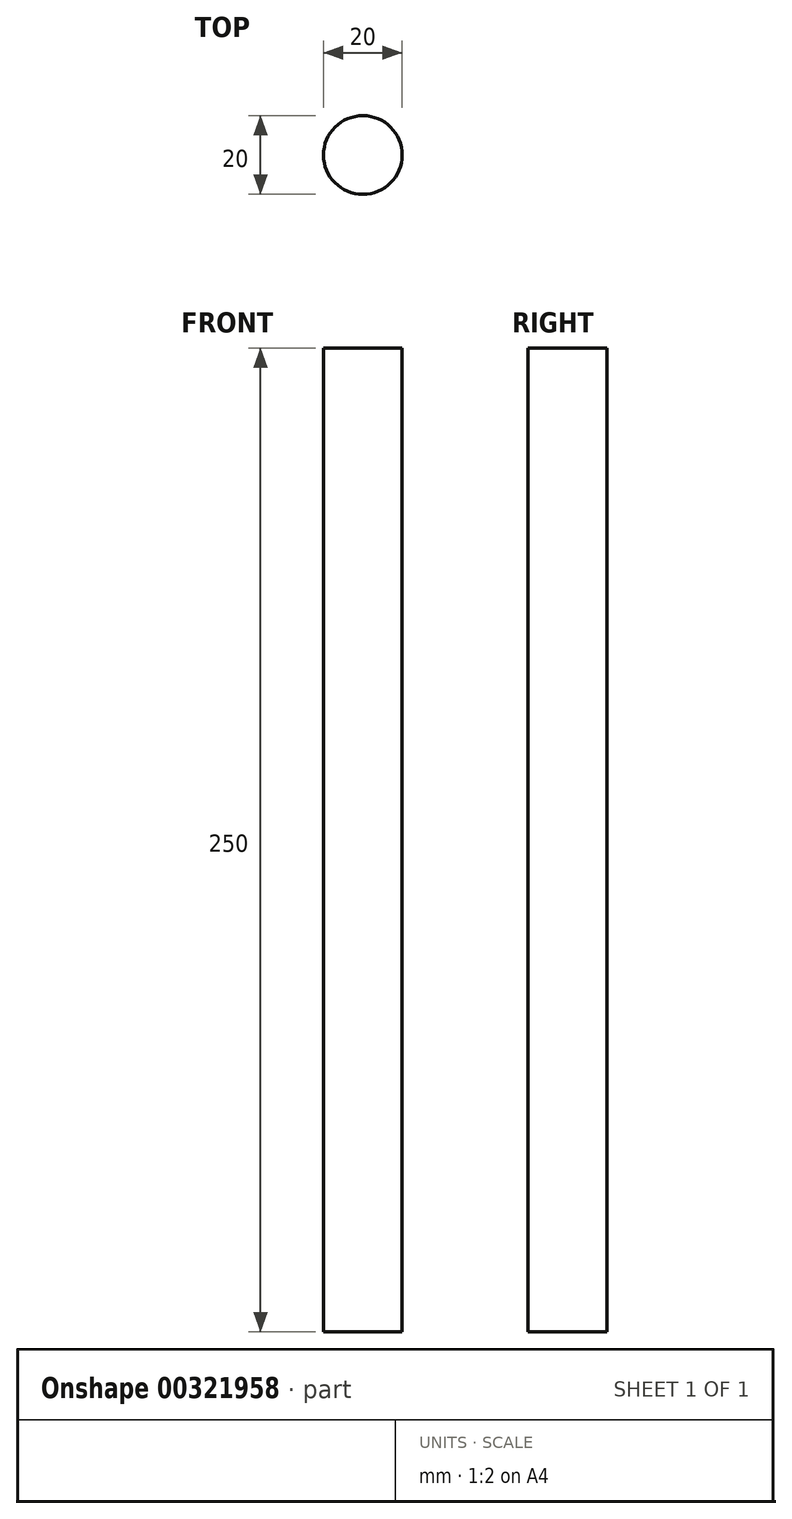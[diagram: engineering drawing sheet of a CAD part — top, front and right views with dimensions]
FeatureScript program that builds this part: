
annotation { "Feature Type Name" : "Feature", "Feature Type Description" : "" }
export const myFeature = defineFeature(function(context is Context, id is Id, definition is map)
    precondition{}
    {
        {
            var Q0;
            Q0=qCreatedBy(makeId("Top.planeOp"),FACE);
            var sketch = newSketch(context, id + "F0", { "sketchPlane" : qUnion([Q0])});
            skCircle(sketch, "E0", {"center": v(0, 0) * mm, "radius": 10 * mm});
            skSolve(sketch);
        }
        {
            var Q0;
            Q0 = qSketchRegion(id + "F0", true);
            extrude(context, id + "F1", {"entities" : qUnion([Q0]), "endBound" : BoundingType.SYMMETRIC, "depth" : 250 * mm});
        }
    });
